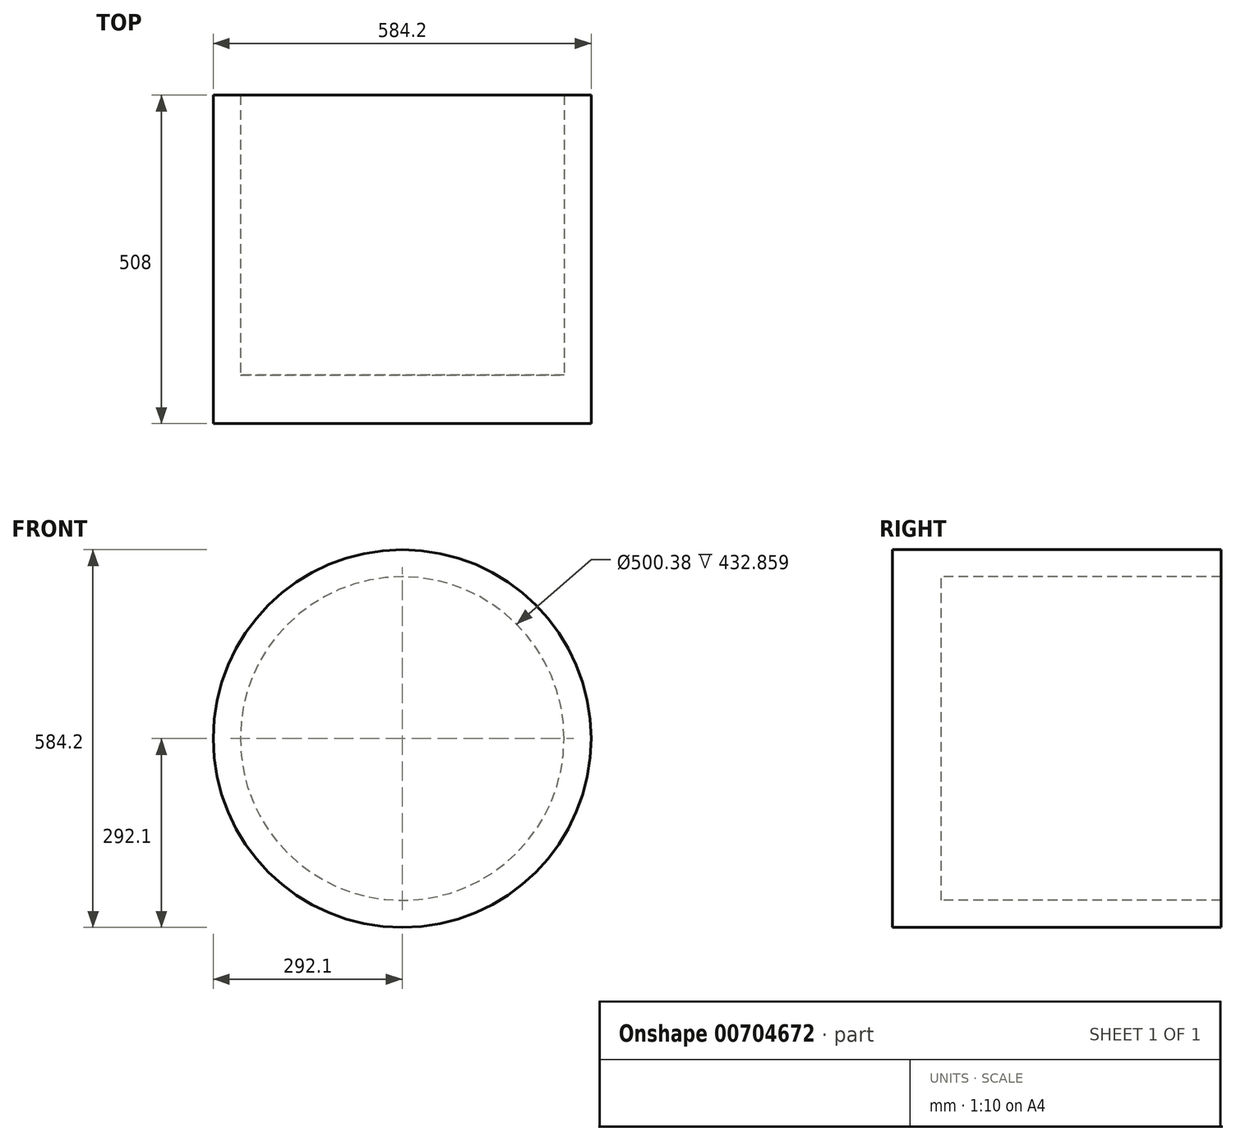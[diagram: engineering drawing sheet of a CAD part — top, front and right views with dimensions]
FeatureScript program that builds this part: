
annotation { "Feature Type Name" : "Feature", "Feature Type Description" : "" }
export const myFeature = defineFeature(function(context is Context, id is Id, definition is map)
    precondition{}
    {
        {
            var Q0;
            Q0=qCreatedBy(makeId("Top.planeOp"),FACE);
            var sketch = newSketch(context, id + "F0", { "sketchPlane" : qUnion([Q0])});
            skLineSegment(sketch, "E0", {"start": v(0, -349.28) * mm, "end": v(0, 158.72) * mm});
            skLineSegment(sketch, "E1", {"start": v(0, 158.72) * mm, "end": v(41.91, 158.72) * mm});
            skLineSegment(sketch, "E2", {"start": v(41.91, 158.72) * mm, "end": v(41.91, -274.14) * mm});
            skLineSegment(sketch, "E3", {"start": v(292.1, -349.28) * mm, "end": v(0, -349.28) * mm});
            skLineSegment(sketch, "E4", {"start": v(41.91, -274.14) * mm, "end": v(292.1, -274.14) * mm});
            skLineSegment(sketch, "E5", {"start": v(292.1, -349.28) * mm, "end": v(292.1, -274.14) * mm});
            skSolve(sketch);
        }
        {
            var Q0;
            Q0 = qSketchRegion(id + "F0", true);
            var Q1;
            Q1=makeQuery(id+"F0.imprint","IMPRINT",FACE,{"disambiguationData":[TD([[makeQuery(id+"F0.imprint","IMPRINT",EDGE,{"derivedFrom":sQuery(id+"F0.wireOp",EDGE,"E0")}),-1.0]])]});
            var Q2;
            Q2=sQuery(id+"F0.wireOp",EDGE,"E5");
            revolve(context, id + "F1", {"surfaceOperationType" : NewSurfaceOperationType.NEW, "entities" : qUnion([Q0, Q1]), "axis" : qUnion([Q2]), "revolveType" : RevolveType.FULL});
        }
    });
